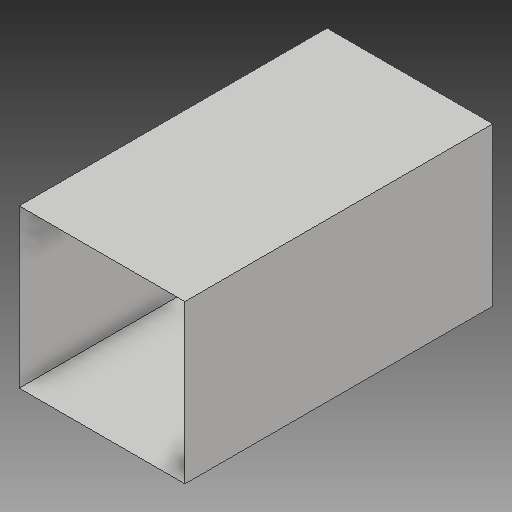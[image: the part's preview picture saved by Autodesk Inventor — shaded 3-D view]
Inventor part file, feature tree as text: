
AUTODESK INVENTOR PART (.ipt)
format: ipt  version: 2017 (Build 210142000, 142)  size: 90,112 bytes
history: native  units: in
note: dims shown in document units (in); Inventor stores cm internally (conversion verified against a paired STEP export)
features: extrude x1, other x1, sketch x1
ambient origin geometry x8: Origin, YZ Plane, XZ Plane, XY Plane, X Axis, Y Axis, Z Axis, Center Point
bodies: Solid1 (feature_tree)
feature tree (3):
  extrude  "corridor"  Depth=7.0in
  other  "removed ends"
  sketch  "Sketch1"  dims[d0=6.6667in d1=7.0in d2=13.0in d3=0.0in]
